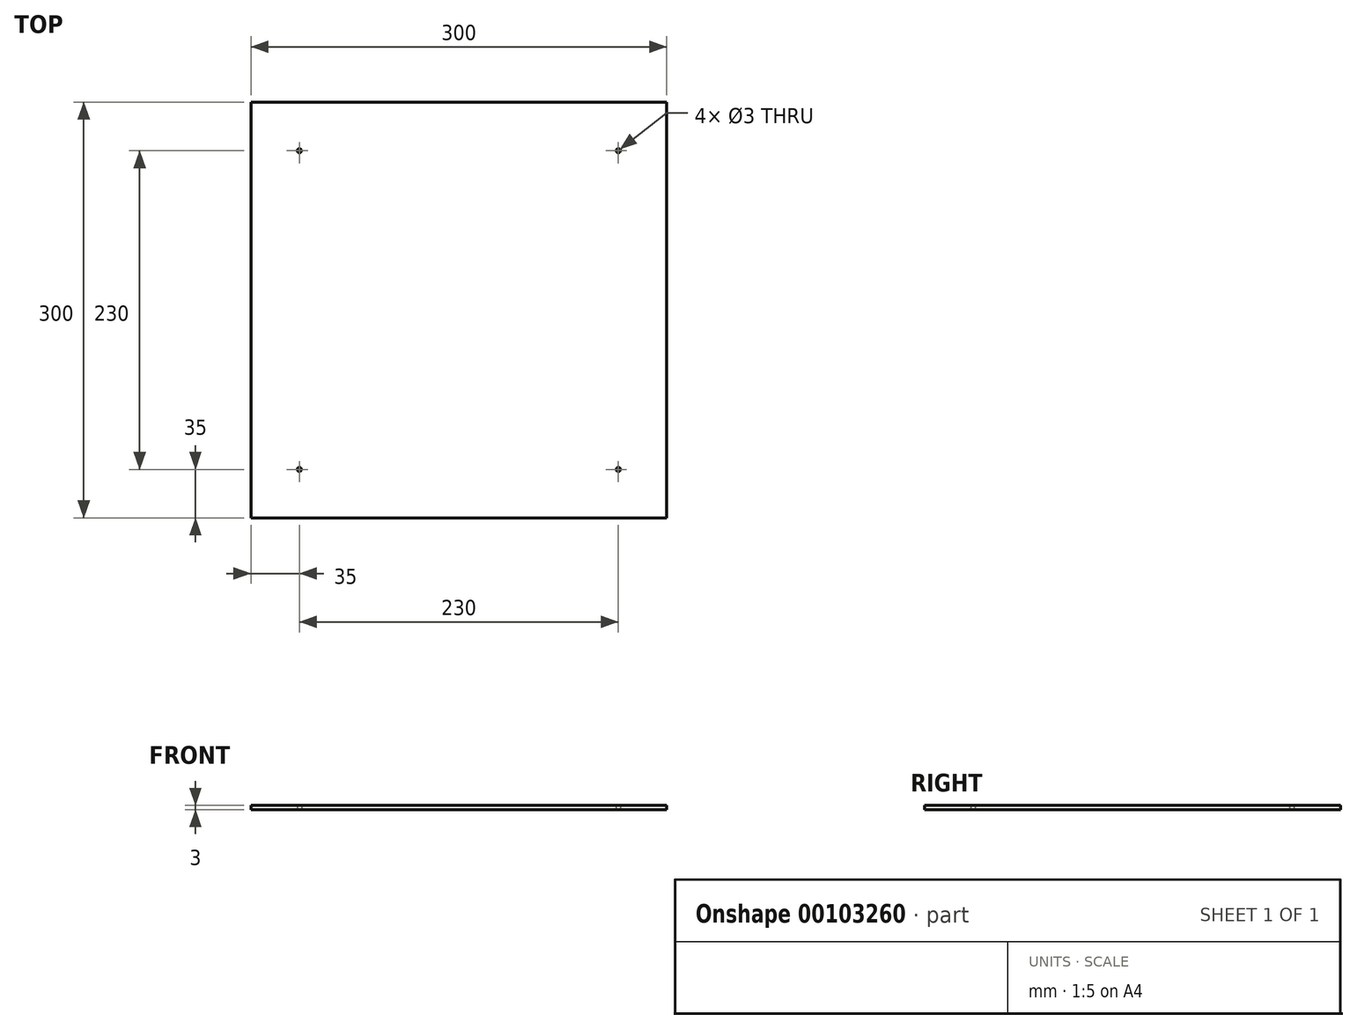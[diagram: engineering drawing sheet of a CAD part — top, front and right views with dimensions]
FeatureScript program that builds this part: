
annotation { "Feature Type Name" : "Feature", "Feature Type Description" : "" }
export const myFeature = defineFeature(function(context is Context, id is Id, definition is map)
    precondition{}
    {
        {
            var Q0;
            Q0=qCreatedBy(makeId("Top.planeOp"),FACE);
            var sketch = newSketch(context, id + "F0", { "sketchPlane" : qUnion([Q0])});
            skLineSegment(sketch, "E0.bottom", {"start": v(150, -150) * mm, "end": v(-150, -150) * mm});
            skLineSegment(sketch, "E0.top", {"start": v(150, 150) * mm, "end": v(-150, 150) * mm});
            skLineSegment(sketch, "E0.left", {"start": v(150, -150) * mm, "end": v(150, 150) * mm});
            skLineSegment(sketch, "E0.right", {"start": v(-150, -150) * mm, "end": v(-150, 150) * mm});
            skPoint(sketch, "E0.middle", {"position": v(0, 0) * mm});
            skCircle(sketch, "E1", {"center": v(115, 115) * mm, "radius": 1.5 * mm});
            skCircle(sketch, "E2.MirrorC", {"center": v(-115, 115) * mm, "radius": 1.5 * mm});
            skCircle(sketch, "E3.MirrorC", {"center": v(115, -115) * mm, "radius": 1.5 * mm});
            skCircle(sketch, "E4.MirrorC", {"center": v(-115, -115) * mm, "radius": 1.5 * mm});
            skSolve(sketch);
        }
        {
            var Q0;
            Q0 = qSketchRegion(id + "F0", true);
            extrude(context, id + "F1", {"entities" : qUnion([Q0]), "depth" : 3 * mm});
        }
    });
